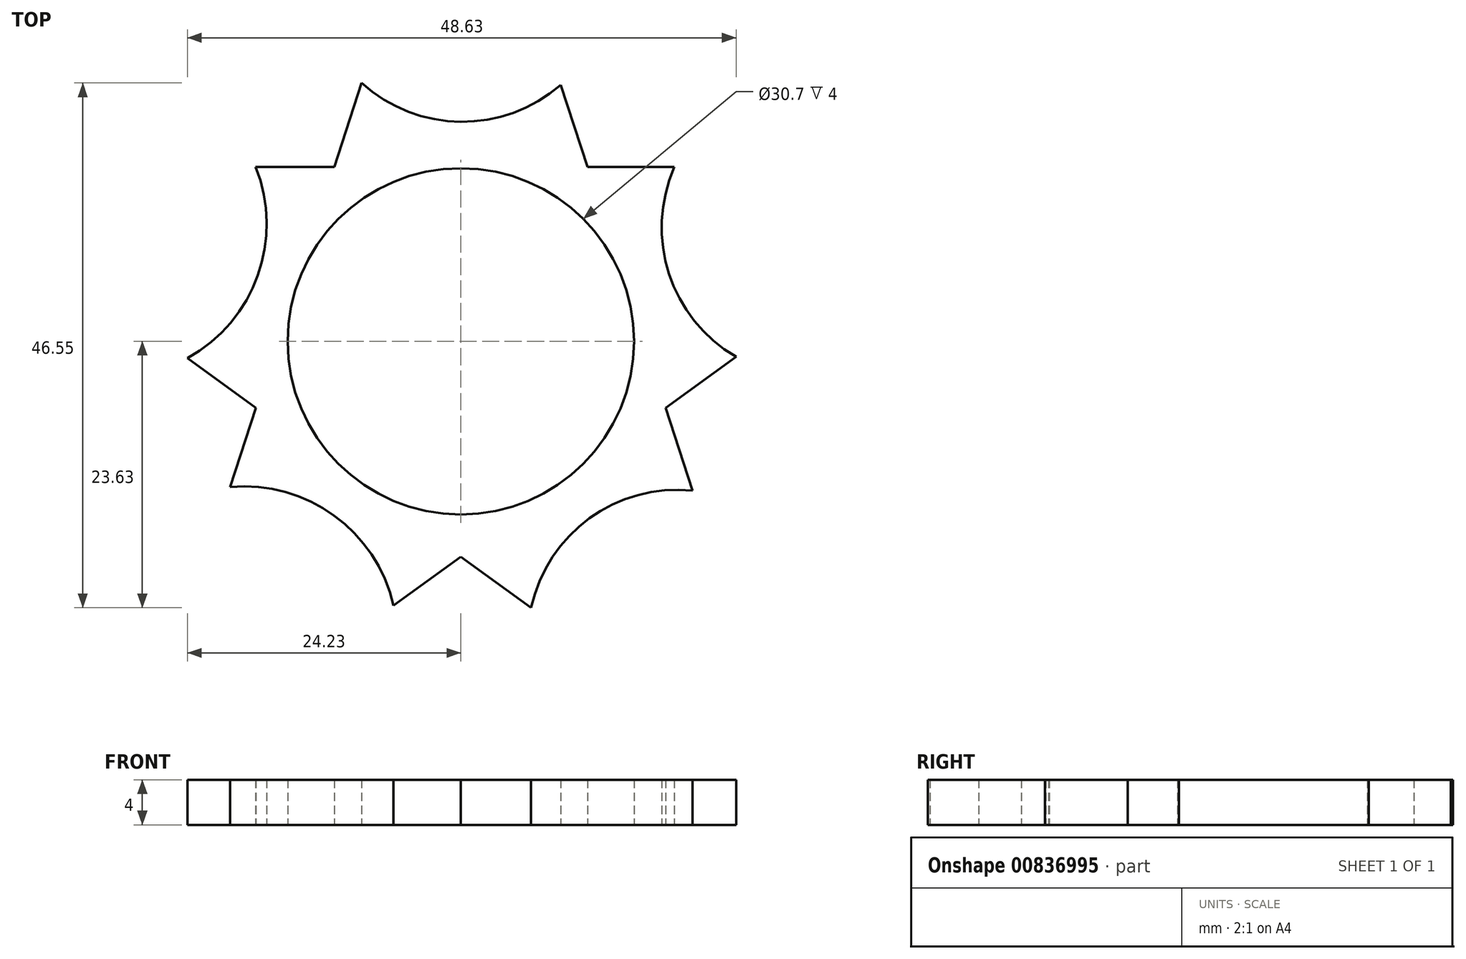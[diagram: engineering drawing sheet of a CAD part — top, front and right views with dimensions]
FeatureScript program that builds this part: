
annotation { "Feature Type Name" : "Feature", "Feature Type Description" : "" }
export const myFeature = defineFeature(function(context is Context, id is Id, definition is map)
    precondition{}
    {
        {
            var Q0;
            Q0=qCreatedBy(makeId("Top.planeOp"),FACE);
            var sketch = newSketch(context, id + "F0", { "sketchPlane" : qUnion([Q0])});
            skCircle(sketch, "E0", {"center": v(0, 0) * mm, "radius": 15.35 * mm});
            skArc(sketch, "E1.cCircle", {"start": v(-29.39, -40.45) * mm, "mid": v(0, -50) * mm, "end": v(29.39, -40.45) * mm, "construction": true});
            skLineSegment(sketch, "E1.2", {"start": v(29.39, -40.45) * mm, "end": v(-29.39, -40.45) * mm, "construction": true});
            skLineSegment(sketch, "E2", {"start": v(-41.1, 10.77) * mm, "end": v(-18.16, -5.9) * mm});
            skLineSegment(sketch, "E3", {"start": v(-29.39, -40.45) * mm, "end": v(-18.16, -5.9) * mm});
            skLineSegment(sketch, "E4", {"start": v(29.39, -40.45) * mm, "end": v(18.16, -5.9) * mm});
            skLineSegment(sketch, "E5", {"start": v(-43.38, 15.45) * mm, "end": v(-11.23, 15.45) * mm});
            skLineSegment(sketch, "E6", {"start": v(-43.8, 14.23) * mm, "end": v(-18, 5.85) * mm});
            skLineSegment(sketch, "E7", {"start": v(0, 50) * mm, "end": v(0, 32.68) * mm});
            skLineSegment(sketch, "E8", {"start": v(-29.39, -40.45) * mm, "end": v(-11.23, -15.45) * mm});
            skLineSegment(sketch, "E9", {"start": v(-9.02, 12.42) * mm, "end": v(9.08, -12.5) * mm});
            skLineSegment(sketch, "E10", {"start": v(-40.63, 13.2) * mm, "end": v(-18, 5.85) * mm});
            skLineSegment(sketch, "E11", {"start": v(-14.6, 4.74) * mm, "end": v(-14.7, 4.77) * mm});
            skCircle(sketch, "E12", {"center": v(-31.08, 10.1) * mm, "radius": 10.05 * mm});
            skLineSegment(sketch, "E13", {"start": v(0, 50) * mm, "end": v(0, 19.48) * mm});
            skLineSegment(sketch, "E14", {"start": v(0, 19.48) * mm, "end": v(0, 32.68) * mm});
            skLineSegment(sketch, "E15", {"start": v(14.6, 4.74) * mm, "end": v(14.7, 4.77) * mm});
            skLineSegment(sketch, "E16", {"start": v(-29.39, -40.45) * mm, "end": v(-9.02, -12.42) * mm});
            skLineSegment(sketch, "E17", {"start": v(-9.02, -12.42) * mm, "end": v(-19.2, -26.43) * mm});
            skLineSegment(sketch, "E18", {"start": v(9.02, -12.42) * mm, "end": v(9.08, -12.5) * mm});
            skCircle(sketch, "E19", {"center": v(-19.2, -26.43) * mm, "radius": 10.05 * mm});
            skCircle(sketch, "E20", {"center": v(0, 32.68) * mm, "radius": 10.05 * mm});
            skArc(sketch, "E21", {"start": v(27.34, 0.77) * mm, "mid": v(27.65, 0.65) * mm, "end": v(27.97, 0.54) * mm});
            skPoint(sketch, "E22", {"position": v(19.2, -26.43) * mm});
            skCircle(sketch, "E23", {"center": v(19.2, -26.43) * mm, "radius": 10.05 * mm});
            skArc(sketch, "E24.cCircle", {"start": v(-33.17, 19.93) * mm, "mid": v(-34.18, 0.54) * mm, "end": v(-23.6, 16.82) * mm, "construction": true});
            skLineSegment(sketch, "E24.0", {"start": v(-21.52, 7) * mm, "end": v(-28.99, 0.27) * mm});
            skLineSegment(sketch, "E24.1", {"start": v(-28.99, 0.27) * mm, "end": v(-38.54, 3.37) * mm});
            skLineSegment(sketch, "E24.2", {"start": v(-38.54, 3.37) * mm, "end": v(-40.63, 13.2) * mm});
            skLineSegment(sketch, "E24.3", {"start": v(-40.63, 13.2) * mm, "end": v(-33.17, 19.93) * mm});
            skLineSegment(sketch, "E24.4", {"start": v(-33.17, 19.93) * mm, "end": v(-23.6, 16.82) * mm});
            skLineSegment(sketch, "E24.5", {"start": v(-23.6, 16.82) * mm, "end": v(-21.52, 7) * mm});
            skCircle(sketch, "E25.cCircle", {"center": v(0, 32.68) * mm, "radius": 10.05 * mm, "construction": true});
            skLineSegment(sketch, "E25.0", {"start": v(0, 22.62) * mm, "end": v(-8.7, 27.65) * mm});
            skLineSegment(sketch, "E25.1", {"start": v(-8.7, 27.65) * mm, "end": v(-8.7, 37.7) * mm});
            skLineSegment(sketch, "E25.2", {"start": v(-8.7, 37.7) * mm, "end": v(0, 42.73) * mm});
            skLineSegment(sketch, "E25.3", {"start": v(0, 42.73) * mm, "end": v(8.7, 37.7) * mm});
            skLineSegment(sketch, "E25.4", {"start": v(8.7, 37.7) * mm, "end": v(8.7, 27.65) * mm});
            skLineSegment(sketch, "E25.5", {"start": v(8.7, 27.65) * mm, "end": v(0, 22.62) * mm});
            skArc(sketch, "E26.cCircle", {"start": v(27.34, 0.77) * mm, "mid": v(28.15, 0.48) * mm, "end": v(28.99, 0.27) * mm, "construction": true});
            skLineSegment(sketch, "E26.0", {"start": v(21.52, 7) * mm, "end": v(23.6, 16.82) * mm});
            skLineSegment(sketch, "E26.1", {"start": v(23.6, 16.82) * mm, "end": v(33.17, 19.93) * mm});
            skLineSegment(sketch, "E26.2", {"start": v(33.17, 19.93) * mm, "end": v(40.63, 13.2) * mm});
            skLineSegment(sketch, "E26.3", {"start": v(40.63, 13.2) * mm, "end": v(38.54, 3.37) * mm});
            skLineSegment(sketch, "E26.4", {"start": v(38.54, 3.37) * mm, "end": v(28.99, 0.27) * mm});
            skLineSegment(sketch, "E26.5", {"start": v(28.99, 0.27) * mm, "end": v(21.52, 7) * mm});
            skCircle(sketch, "E27.cCircle", {"center": v(-19.2, -26.43) * mm, "radius": 10.05 * mm, "construction": true});
            skLineSegment(sketch, "E27.0", {"start": v(-13.3, -18.3) * mm, "end": v(-9.21, -27.49) * mm});
            skLineSegment(sketch, "E27.1", {"start": v(-9.21, -27.49) * mm, "end": v(-15.12, -35.62) * mm});
            skLineSegment(sketch, "E27.2", {"start": v(-15.12, -35.62) * mm, "end": v(-25.11, -34.57) * mm});
            skLineSegment(sketch, "E27.3", {"start": v(-25.11, -34.57) * mm, "end": v(-29.2, -25.38) * mm});
            skLineSegment(sketch, "E27.4", {"start": v(-29.2, -25.38) * mm, "end": v(-23.3, -17.25) * mm});
            skLineSegment(sketch, "E27.5", {"start": v(-23.3, -17.25) * mm, "end": v(-13.3, -18.3) * mm});
            skCircle(sketch, "E28.cCircle", {"center": v(19.2, -26.43) * mm, "radius": 10.05 * mm, "construction": true});
            skLineSegment(sketch, "E28.0", {"start": v(13.3, -18.3) * mm, "end": v(23.3, -17.25) * mm});
            skLineSegment(sketch, "E28.1", {"start": v(23.3, -17.25) * mm, "end": v(29.2, -25.38) * mm});
            skLineSegment(sketch, "E28.2", {"start": v(29.2, -25.38) * mm, "end": v(25.11, -34.57) * mm});
            skLineSegment(sketch, "E28.3", {"start": v(25.11, -34.57) * mm, "end": v(15.12, -35.62) * mm});
            skLineSegment(sketch, "E28.4", {"start": v(15.12, -35.62) * mm, "end": v(9.21, -27.49) * mm});
            skLineSegment(sketch, "E28.5", {"start": v(9.21, -27.49) * mm, "end": v(13.3, -18.3) * mm});
            skLineSegment(sketch, "E29", {"start": v(19.2, -26.43) * mm, "end": v(23.3, -13.81) * mm});
            skLineSegment(sketch, "E30", {"start": v(0.13, 32.78) * mm, "end": v(-8.13, 26.77) * mm});
            skLineSegment(sketch, "E31", {"start": v(-30.78, 10.4) * mm, "end": v(-26.71, -2.56) * mm});
            skLineSegment(sketch, "E32", {"start": v(-19.2, -26.43) * mm, "end": v(-5.63, -26.43) * mm});
            skArc(sketch, "E33", {"start": v(-21.31, 20.12) * mm, "mid": v(-13, 15.98) * mm, "end": v(-10.63, 24.96) * mm, "construction": true});
            skArc(sketch, "E34", {"start": v(11.29, 25.53) * mm, "mid": v(9.76, 22.73) * mm, "end": v(9.9, 19.55) * mm, "construction": true});
            skCircle(sketch, "E35", {"center": v(-30.78, 10.4) * mm, "radius": 13.57 * mm});
            skCircle(sketch, "E36", {"center": v(0.13, 32.78) * mm, "radius": 13.3 * mm});
            skArc(sketch, "E37", {"start": v(24.4, -1.37) * mm, "mid": v(43.7, 14.2) * mm, "end": v(18.93, 15.45) * mm});
            skCircle(sketch, "E38", {"center": v(19.2, -26.43) * mm, "radius": 13.27 * mm});
            skCircle(sketch, "E39", {"center": v(-19.2, -26.43) * mm, "radius": 13.57 * mm});
            skLineSegment(sketch, "E40.trimOffspring", {"start": v(-14.7, 4.77) * mm, "end": v(14.6, -4.74) * mm});
            skLineSegment(sketch, "E41.trimOffspring", {"start": v(-11.23, 15.45) * mm, "end": v(0, 50) * mm});
            skLineSegment(sketch, "E42.trimOffspring", {"start": v(11.23, 15.45) * mm, "end": v(15.54, 15.45) * mm});
            skLineSegment(sketch, "E43.trimOffspring", {"start": v(11.23, 15.45) * mm, "end": v(0, 50) * mm});
            skLineSegment(sketch, "E44.trimOffspring", {"start": v(0, 15.35) * mm, "end": v(0, -15.35) * mm});
            skLineSegment(sketch, "E45.trimOffspring", {"start": v(14.7, 4.77) * mm, "end": v(-14.6, -4.74) * mm});
            skLineSegment(sketch, "E46.trimOffspring", {"start": v(14.7, 4.77) * mm, "end": v(14.6, 4.74) * mm});
            skCircle(sketch, "E47", {"center": v(31.08, 10.1) * mm, "radius": 13.27 * mm});
            skLineSegment(sketch, "E48", {"start": v(18.93, 15.45) * mm, "end": v(15.54, 15.45) * mm});
            skPoint(sketch, "E49.orphan", {"position": v(47.55, 15.45) * mm});
            skPoint(sketch, "E1.3.end.orphan", {"position": v(-47.55, 15.45) * mm});
            skLineSegment(sketch, "E50.trimOffspring", {"start": v(5.94, -26.43) * mm, "end": v(19.2, -26.43) * mm});
            skArc(sketch, "E51.trimOffspring", {"start": v(-5.72, -24.86) * mm, "mid": v(-5.94, -26.43) * mm, "end": v(-5.72, -28) * mm, "construction": true});
            skPoint(sketch, "E52.center.orphan", {"position": v(-25, -8.02) * mm});
            skLineSegment(sketch, "E53.trimOffspring", {"start": v(-23.28, -13.49) * mm, "end": v(-19.2, -26.43) * mm});
            skLineSegment(sketch, "E54.trimOffspring", {"start": v(27.97, 0.54) * mm, "end": v(28.13, 1.04) * mm});
            skLineSegment(sketch, "E55.trimOffspring", {"start": v(15.54, 21.39) * mm, "end": v(0, 32.68) * mm});
            skLineSegment(sketch, "E56.trimOffspring", {"start": v(-19.76, 18.32) * mm, "end": v(-31.08, 10.1) * mm});
            skPoint(sketch, "E57.center.orphan", {"position": v(25.14, -8.17) * mm});
            skLineSegment(sketch, "E58.trimOffspring", {"start": v(24.4, -1.37) * mm, "end": v(18.16, -5.9) * mm});
            skLineSegment(sketch, "E59.trimOffspring", {"start": v(0, -19.1) * mm, "end": v(-29.39, -40.45) * mm});
            skLineSegment(sketch, "E60.trimOffspring", {"start": v(11.4, -15.7) * mm, "end": v(29.39, -40.45) * mm});
            skLineSegment(sketch, "E61.trimOffspring", {"start": v(0, -19.1) * mm, "end": v(29.39, -40.45) * mm});
            skLineSegment(sketch, "E62.trimOffspring", {"start": v(-9.08, -12.5) * mm, "end": v(9.02, 12.42) * mm});
            skLineSegment(sketch, "E63.trimOffspring", {"start": v(-18, 5.85) * mm, "end": v(-31.08, 10.1) * mm});
            skLineSegment(sketch, "E64.trimOffspring", {"start": v(-14.7, 4.77) * mm, "end": v(-14.6, 4.74) * mm});
            skSolve(sketch);
        }
        {
            var Q0;
            {var subQ45=sQuery(id+"F0.wireOp",EDGE,"E42.trimOffspring");Q0=makeQuery(id+"F0.imprint","IMPRINT",FACE,{"disambiguationData":[TD([[makeQuery(id+"F0.imprint","IMPRINT",EDGE,{"derivedFrom":subQ45}),-1.0]])]});}
            var Q1;
            Q1 = qSketchRegion(id + "F2", true);
            extrude(context, id + "F1", {"entities" : qUnion([Q0, Q1]), "depth" : 4 * mm, "offsetDistance" : 25 * mm});
        }
    });
